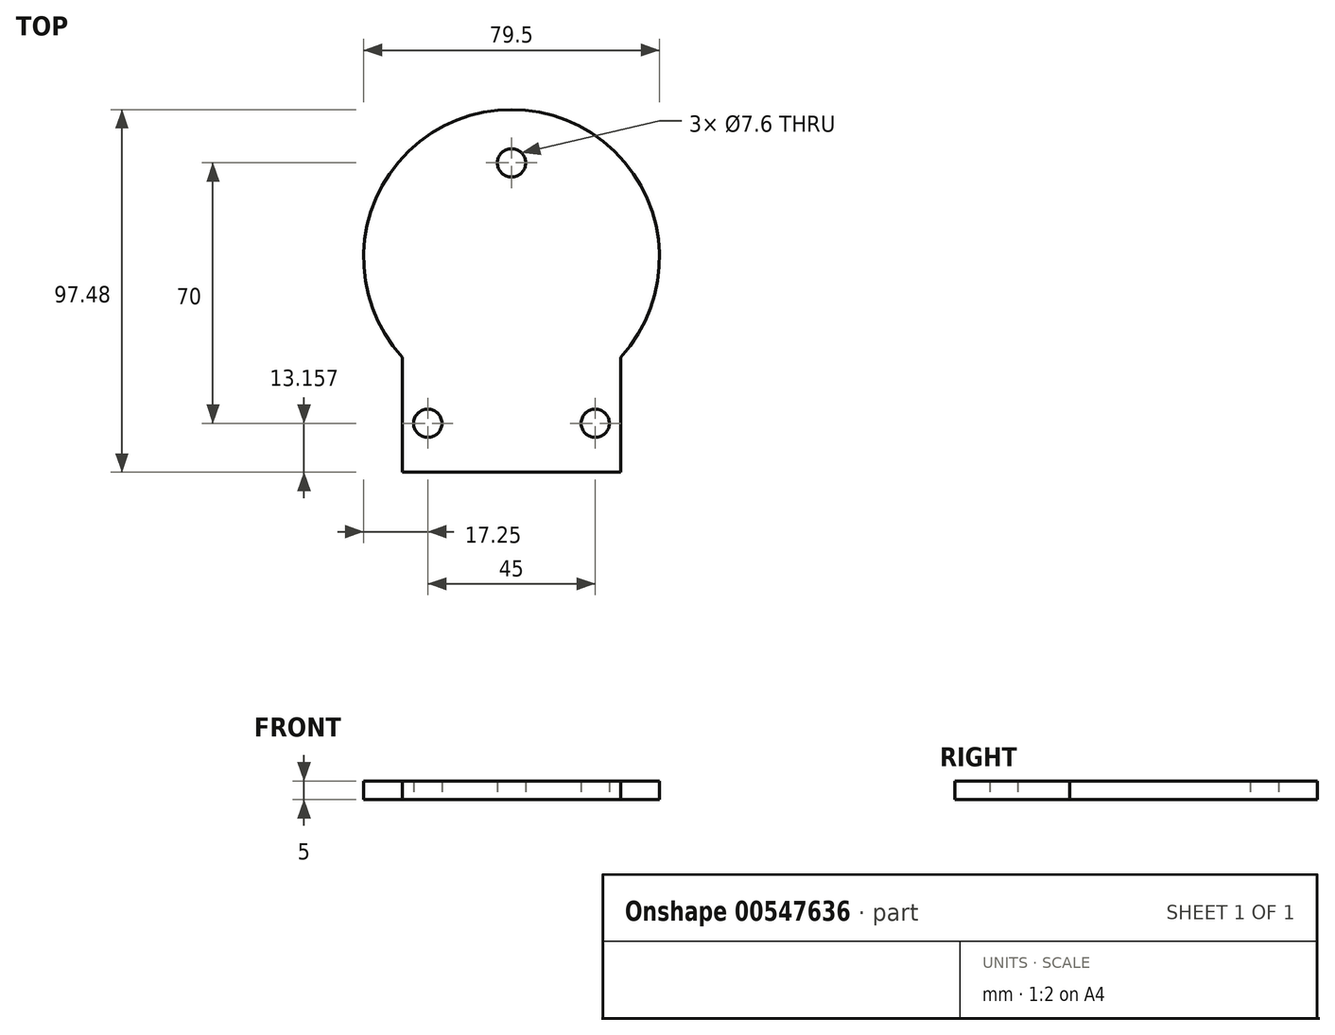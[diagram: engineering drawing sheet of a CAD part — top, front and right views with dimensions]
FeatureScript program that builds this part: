
annotation { "Feature Type Name" : "Feature", "Feature Type Description" : "" }
export const myFeature = defineFeature(function(context is Context, id is Id, definition is map)
    precondition{}
    {
        {
            var Q0;
            Q0=qCreatedBy(makeId("Top.planeOp"),FACE);
            var sketch = newSketch(context, id + "F0", { "sketchPlane" : qUnion([Q0])});
            skArc(sketch, "E0", {"start": v(29.34, -26.82) * mm, "mid": v(0, 39.75) * mm, "end": v(-29.34, -26.82) * mm});
            skLineSegment(sketch, "E1.top", {"start": v(29.34, -57.73) * mm, "end": v(-29.34, -57.73) * mm});
            skLineSegment(sketch, "E1.left", {"start": v(29.34, -26.82) * mm, "end": v(29.34, -57.73) * mm});
            skLineSegment(sketch, "E1.right", {"start": v(-29.34, -26.82) * mm, "end": v(-29.34, -57.73) * mm});
            skPoint(sketch, "E2", {"position": v(0, -57.73) * mm});
            skCircle(sketch, "E3", {"center": v(-22.5, -44.57) * mm, "radius": 3.8 * mm});
            skCircle(sketch, "E4", {"center": v(22.5, -44.57) * mm, "radius": 3.8 * mm});
            skCircle(sketch, "E5", {"center": v(0, 25.43) * mm, "radius": 3.8 * mm});
            skLineSegment(sketch, "E6", {"start": v(22.5, -44.57) * mm, "end": v(-22.5, -44.57) * mm, "construction": true});
            skPoint(sketch, "E7", {"position": v(0, -44.57) * mm});
            skSolve(sketch);
        }
        {
            var Q0;
            Q0=makeQuery(id+"F0.imprint","IMPRINT",FACE,{"disambiguationData":[TD([[makeQuery(id+"F0.imprint","IMPRINT",EDGE,{"derivedFrom":sQuery(id+"F0.wireOp",EDGE,"E0")}),1.0]])]});
            extrude(context, id + "F1", {"entities" : qUnion([Q0]), "depth" : 5 * mm, "offsetDistance" : 25 * mm});
        }
    });
